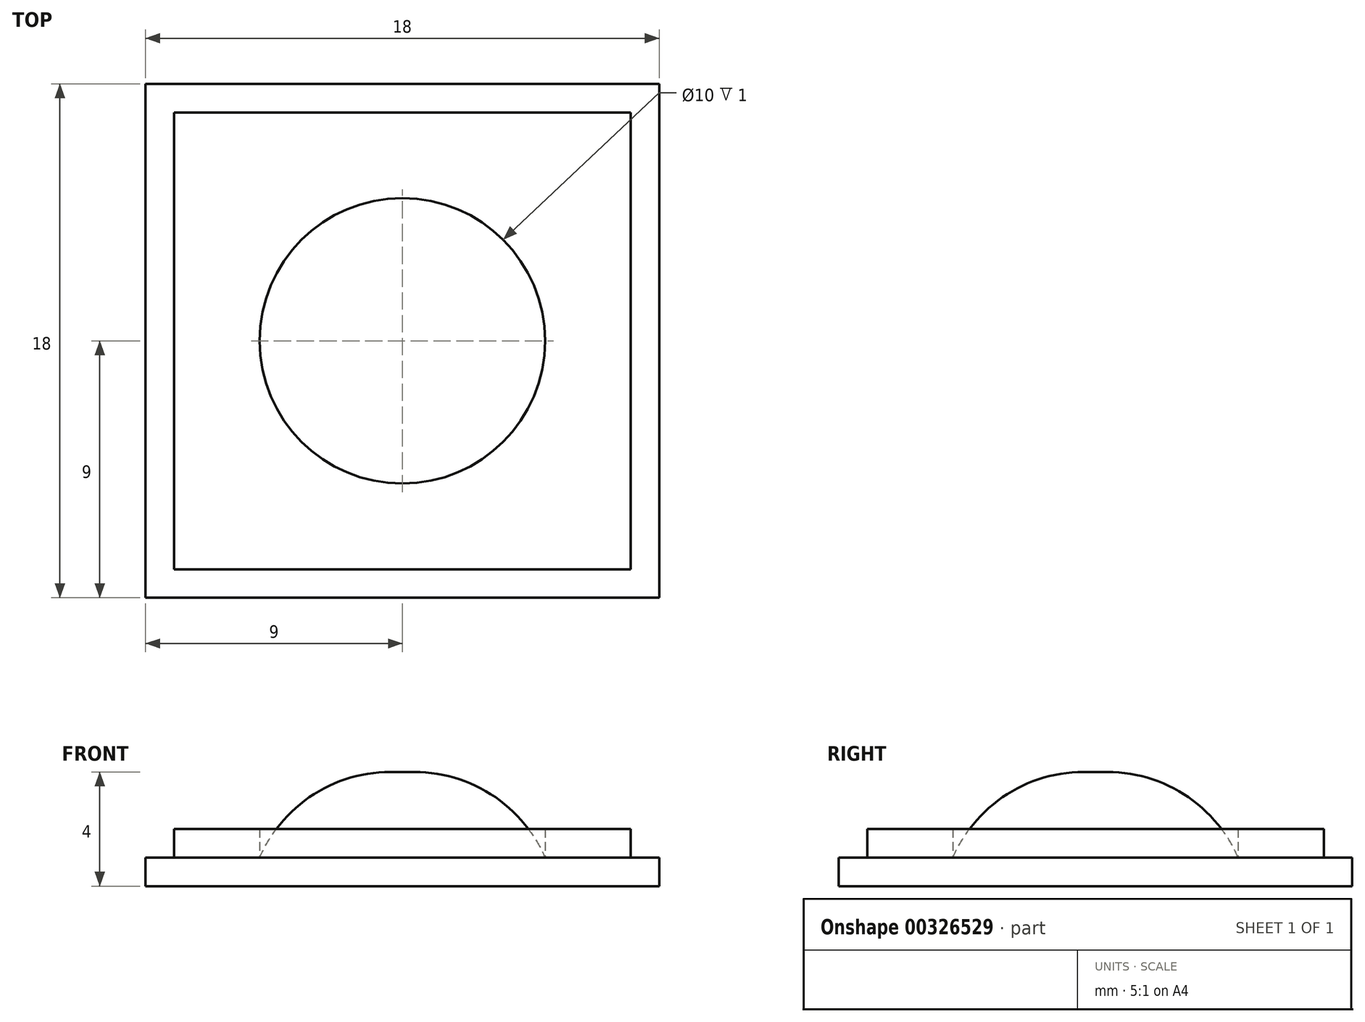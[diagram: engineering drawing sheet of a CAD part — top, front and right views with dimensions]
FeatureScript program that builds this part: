
annotation { "Feature Type Name" : "Feature", "Feature Type Description" : "" }
export const myFeature = defineFeature(function(context is Context, id is Id, definition is map)
    precondition{}
    {
        {
            var Q0;
            Q0=qCreatedBy(makeId("Top.planeOp"),FACE);
            var sketch = newSketch(context, id + "F0", { "sketchPlane" : qUnion([Q0])});
            skLineSegment(sketch, "E0.bottom", {"start": v(9, 9) * mm, "end": v(-9, 9) * mm});
            skLineSegment(sketch, "E0.top", {"start": v(9, -9) * mm, "end": v(-9, -9) * mm});
            skLineSegment(sketch, "E0.left", {"start": v(9, 9) * mm, "end": v(9, -9) * mm});
            skLineSegment(sketch, "E0.right", {"start": v(-9, 9) * mm, "end": v(-9, -9) * mm});
            skPoint(sketch, "E0.middle", {"position": v(0, 0) * mm});
            skLineSegment(sketch, "E1.0", {"start": v(8, 8) * mm, "end": v(-8, 8) * mm});
            skLineSegment(sketch, "E1.1", {"start": v(8, 8) * mm, "end": v(8, -8) * mm});
            skLineSegment(sketch, "E1.2", {"start": v(8, -8) * mm, "end": v(-8, -8) * mm});
            skLineSegment(sketch, "E1.3", {"start": v(-8, 8) * mm, "end": v(-8, -8) * mm});
            skCircle(sketch, "E2", {"center": v(0, 0) * mm, "radius": 5 * mm});
            skSolve(sketch);
        }
        {
            var Q0;
            Q0=makeQuery(id+"F0.imprint","IMPRINT",FACE,{"disambiguationData":[TD([[makeQuery(id+"F0.imprint","IMPRINT",EDGE,{"derivedFrom":sQuery(id+"F0.wireOp",EDGE,"E0.bottom")}),1.0]])]});
            var Q1;
            Q1=makeQuery(id+"F0.imprint","IMPRINT",FACE,{"disambiguationData":[TD([[makeQuery(id+"F0.imprint","IMPRINT",EDGE,{"derivedFrom":sQuery(id+"F0.wireOp",EDGE,"E1.0")}),1.0]])]});
            var Q2;
            Q2=makeQuery(id+"F0.imprint","IMPRINT",FACE,{"disambiguationData":[TD([[makeQuery(id+"F0.imprint","IMPRINT",EDGE,{"derivedFrom":sQuery(id+"F0.wireOp",EDGE,"E2")}),1.0]])]});
            extrude(context, id + "F1", {"entities" : qUnion([Q0, Q1, Q2]), "oppositeDirection" : true, "depth" : 1 * mm});
        }
        {
            var Q0;
            Q0=makeQuery(id+"F0.imprint","IMPRINT",FACE,{"disambiguationData":[TD([[makeQuery(id+"F0.imprint","IMPRINT",EDGE,{"derivedFrom":sQuery(id+"F0.wireOp",EDGE,"E1.0")}),1.0]])]});
            extrude(context, id + "F2", {"entities" : qUnion([Q0]), "operationType" : NewBodyOperationType.ADD, "depth" : 1 * mm});
        }
        {
            var Q0;
            Q0=makeQuery(id+"F0.imprint","IMPRINT",FACE,{"disambiguationData":[TD([[makeQuery(id+"F0.imprint","IMPRINT",EDGE,{"derivedFrom":sQuery(id+"F0.wireOp",EDGE,"E2")}),1.0]])]});
            extrude(context, id + "F3", {"entities" : qUnion([Q0]), "depth" : 3 * mm});
        }
        {
            var Q0;
            Q0=makeQuery(id+"F3.opExtrude","CAP_EDGE",EDGE,{"disambiguationData":[OSD([sQuery(id+"F0.wireOp",EDGE,"E2")])],"isStart":false});
            fillet(context, id + "F4", {"entities" : qUnion([Q0]), "radius" : 5 * mm, "tangentPropagation" : true, "allowEdgeOverflow" : false});
        }
    });
